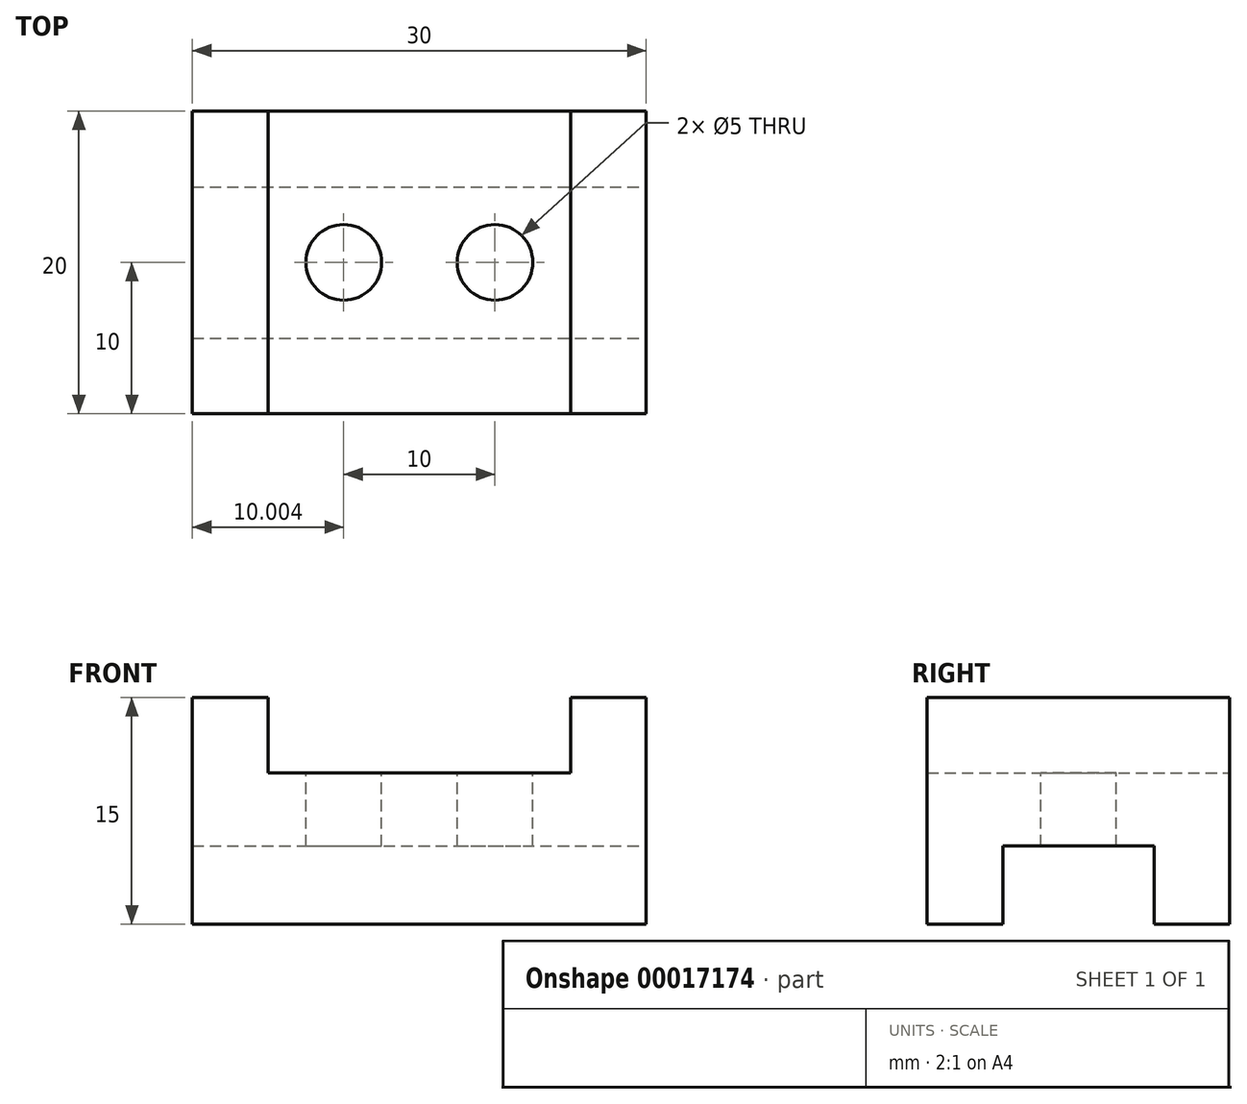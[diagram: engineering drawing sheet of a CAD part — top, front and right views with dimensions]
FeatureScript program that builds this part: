
annotation { "Feature Type Name" : "Feature", "Feature Type Description" : "" }
export const myFeature = defineFeature(function(context is Context, id is Id, definition is map)
    precondition{}
    {
        {
            var Q0;
            Q0=qCreatedBy(makeId("Front.planeOp"),FACE);
            var sketch = newSketch(context, id + "F0", { "sketchPlane" : qUnion([Q0])});
            skLineSegment(sketch, "E0.bottom", {"start": v(4.07, 15) * mm, "end": v(34.07, 15) * mm});
            skLineSegment(sketch, "E0.top", {"start": v(4.07, 0) * mm, "end": v(34.07, 0) * mm});
            skLineSegment(sketch, "E0.left", {"start": v(4.07, 15) * mm, "end": v(4.07, 0) * mm});
            skLineSegment(sketch, "E0.right", {"start": v(34.07, 15) * mm, "end": v(34.07, 0) * mm});
            skSolve(sketch);
        }
        {
            var Q0;
            Q0=makeQuery(id+"F0.imprint","IMPRINT",FACE,{"disambiguationData":[TD([[makeQuery(id+"F0.imprint","IMPRINT",EDGE,{"derivedFrom":sQuery(id+"F0.wireOp",EDGE,"E0.bottom")}),-1.0]])]});
            extrude(context, id + "F1", {"entities" : qUnion([Q0]), "depth" : 20 * mm});
        }
        {
            var Q0;
            Q0=makeQuery(id+"F1.opExtrude","SWEPT_FACE",FACE,{"disambiguationData":[OSD([sQuery(id+"F0.wireOp",EDGE,"E0.bottom")])]});
            var sketch = newSketch(context, id + "F2", { "sketchPlane" : qUnion([Q0])});
            skLineSegment(sketch, "E1.bottom", {"start": v(9.07, -20) * mm, "end": v(29.07, -20) * mm});
            skLineSegment(sketch, "E1.top", {"start": v(9.07, 0) * mm, "end": v(29.07, 0) * mm});
            skLineSegment(sketch, "E1.left", {"start": v(9.07, -20) * mm, "end": v(9.07, 0) * mm});
            skLineSegment(sketch, "E1.right", {"start": v(29.07, -20) * mm, "end": v(29.07, 0) * mm});
            skSolve(sketch);
        }
        {
            var Q0;
            Q0=makeQuery(id+"F2.imprint","IMPRINT",FACE,{"disambiguationData":[TD([[makeQuery(id+"F2.imprint","IMPRINT",EDGE,{"derivedFrom":sQuery(id+"F2.wireOp",EDGE,"E1.bottom")}),1.0]])]});
            extrude(context, id + "F3", {"entities" : qUnion([Q0]), "operationType" : NewBodyOperationType.REMOVE, "oppositeDirection" : true, "depth" : 5 * mm});
        }
        {
            var Q0;
            Q0=makeQuery(id+"F3.boolean.opBoolean","COPY",FACE,{"derivedFrom":makeQuery(id+"F3.opExtrude","CAP_FACE",FACE,{"disambiguationData":[OSD([sQuery(id+"F2.wireOp",EDGE,"E1.bottom"),sQuery(id+"F2.wireOp",EDGE,"E1.top"),sQuery(id+"F2.wireOp",EDGE,"E1.left"),sQuery(id+"F2.wireOp",EDGE,"E1.right")])],"isStart":false})});
            var sketch = newSketch(context, id + "F4", { "sketchPlane" : qUnion([Q0])});
            skCircle(sketch, "E2", {"center": v(14.07, -10) * mm, "radius": 2.5 * mm});
            skLineSegment(sketch, "E3", {"start": v(9.07, -10) * mm, "end": v(14.07, -10) * mm});
            skLineSegment(sketch, "E4", {"start": v(29.07, -10) * mm, "end": v(24.07, -10) * mm});
            skCircle(sketch, "E5", {"center": v(24.07, -10) * mm, "radius": 2.5 * mm});
            skSolve(sketch);
        }
        {
            var Q0;
            Q0=makeQuery(id+"F4.imprint","IMPRINT",FACE,{"disambiguationData":[TD([[makeQuery(id+"F4.imprint","IMPRINT",EDGE,{"derivedFrom":sQuery(id+"F4.wireOp",EDGE,"E2")}),1.0]])]});
            var Q1;
            Q1=makeQuery(id+"F4.imprint","IMPRINT",FACE,{"disambiguationData":[TD([[makeQuery(id+"F4.imprint","IMPRINT",EDGE,{"derivedFrom":sQuery(id+"F4.wireOp",EDGE,"E5")}),1.0]])]});
            extrude(context, id + "F5", {"entities" : qUnion([Q0, Q1]), "operationType" : NewBodyOperationType.REMOVE, "oppositeDirection" : true, "depth" : 25 * mm});
        }
        {
            var Q0;
            Q0=makeQuery(id+"F1.opExtrude","SWEPT_FACE",FACE,{"disambiguationData":[OSD([sQuery(id+"F0.wireOp",EDGE,"E0.right")])]});
            var sketch = newSketch(context, id + "F6", { "sketchPlane" : qUnion([Q0])});
            skLineSegment(sketch, "E6.bottom", {"start": v(-15, 5.16) * mm, "end": v(-5, 5.16) * mm});
            skLineSegment(sketch, "E6.top", {"start": v(-15, 0) * mm, "end": v(-5, 0) * mm});
            skLineSegment(sketch, "E6.left", {"start": v(-15, 5.16) * mm, "end": v(-15, 0) * mm});
            skLineSegment(sketch, "E6.right", {"start": v(-5, 5.16) * mm, "end": v(-5, 0) * mm});
            skLineSegment(sketch, "E7", {"start": v(-20, 0) * mm, "end": v(-15, 0) * mm});
            skLineSegment(sketch, "E8", {"start": v(0, 0) * mm, "end": v(-5, 0) * mm});
            skSolve(sketch);
        }
        {
            var Q0;
            Q0=makeQuery(id+"F6.imprint","IMPRINT",FACE,{"disambiguationData":[TD([[makeQuery(id+"F6.imprint","IMPRINT",EDGE,{"derivedFrom":sQuery(id+"F6.wireOp",EDGE,"E6.bottom")}),-1.0]])]});
            extrude(context, id + "F7", {"entities" : qUnion([Q0]), "operationType" : NewBodyOperationType.REMOVE, "endBound" : BoundingType.THROUGH_ALL, "oppositeDirection" : true, "depth" : 25 * mm});
        }
    });
